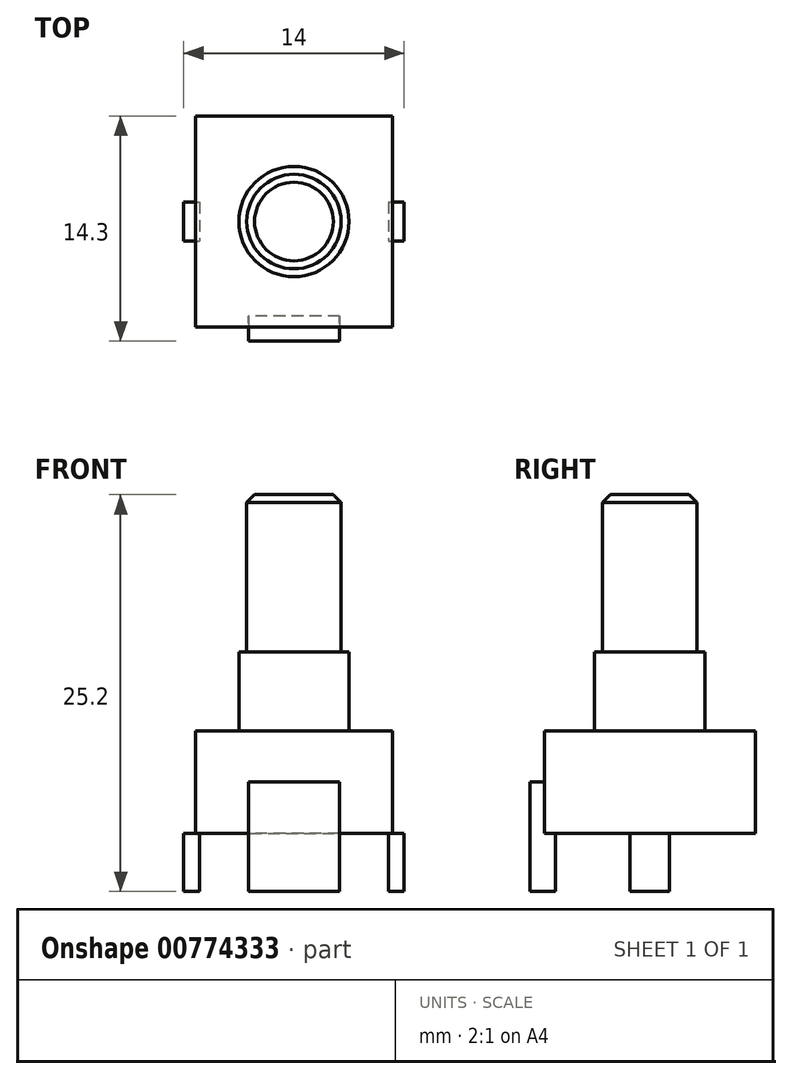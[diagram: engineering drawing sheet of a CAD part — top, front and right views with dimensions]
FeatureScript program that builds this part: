
annotation { "Feature Type Name" : "Feature", "Feature Type Description" : "" }
export const myFeature = defineFeature(function(context is Context, id is Id, definition is map)
    precondition{}
    {
        {
            var Q0;
            Q0=qCreatedBy(makeId("Top.planeOp"),FACE);
            var sketch = newSketch(context, id + "F0", { "sketchPlane" : qUnion([Q0])});
            skLineSegment(sketch, "E0", {"start": v(-6.25, 11.7) * mm, "end": v(0, 11.7) * mm});
            skLineSegment(sketch, "E1", {"start": v(0, 11.7) * mm, "end": v(6.25, 11.7) * mm});
            skLineSegment(sketch, "E2", {"start": v(6.25, 11.7) * mm, "end": v(6.25, 5) * mm});
            skLineSegment(sketch, "E3", {"start": v(6.25, 5) * mm, "end": v(6.25, -1.7) * mm});
            skLineSegment(sketch, "E4", {"start": v(-6.25, 11.7) * mm, "end": v(-6.25, -1.7) * mm});
            skLineSegment(sketch, "E5", {"start": v(-6.25, -1.7) * mm, "end": v(6.25, -1.7) * mm});
            skPoint(sketch, "E6", {"position": v(0, 5) * mm});
            skSolve(sketch);
        }
        {
            var Q0;
            Q0=qCreatedBy(makeId("Top.planeOp"),FACE);
            var sketch = newSketch(context, id + "F1", { "sketchPlane" : qUnion([Q0])});
            skCircle(sketch, "E7", {"center": v(0, 5) * mm, "radius": 3.5 * mm});
            skSolve(sketch);
        }
        {
            var Q0;
            Q0=qCreatedBy(makeId("Top.planeOp"),FACE);
            var sketch = newSketch(context, id + "F2", { "sketchPlane" : qUnion([Q0])});
            skCircle(sketch, "E8", {"center": v(0, 5) * mm, "radius": 3 * mm});
            skSolve(sketch);
        }
        {
            var Q0;
            Q0 = qSketchRegion(id + "F0", true);
            extrude(context, id + "F3", {"entities" : qUnion([Q0]), "depth" : 6.5 * mm, "offsetDistance" : 25 * mm});
        }
        {
            var Q0;
            Q0 = qSketchRegion(id + "F1", true);
            extrude(context, id + "F4", {"entities" : qUnion([Q0]), "operationType" : NewBodyOperationType.ADD, "depth" : (6.5 + 5) * mm, "offsetDistance" : 25 * mm});
        }
        {
            var Q0;
            Q0 = qSketchRegion(id + "F2", true);
            extrude(context, id + "F5", {"entities" : qUnion([Q0]), "operationType" : NewBodyOperationType.ADD, "depth" : (6.5 + 15) * mm, "offsetDistance" : 25 * mm});
        }
        {
            var Q0;
            Q0=makeQuery(id+"F5.opExtrude","CAP_EDGE",EDGE,{"disambiguationData":[OSD([sQuery(id+"F2.wireOp",EDGE,"E8")])],"isStart":false});
            chamfer(context, id + "F6", {"entities" : qUnion([Q0]), "width" : 0.5 * mm, "tangentPropagation" : true});
        }
        {
            var Q0;
            Q0=qCreatedBy(makeId("Top.planeOp"),FACE);
            var sketch = newSketch(context, id + "F7", { "sketchPlane" : qUnion([Q0])});
            skLineSegment(sketch, "E9.bottom", {"start": v(-7, 6.25) * mm, "end": v(-6, 6.25) * mm});
            skLineSegment(sketch, "E9.top", {"start": v(-7, 3.75) * mm, "end": v(-6, 3.75) * mm});
            skLineSegment(sketch, "E9.left", {"start": v(-7, 6.25) * mm, "end": v(-7, 3.75) * mm});
            skLineSegment(sketch, "E9.right", {"start": v(-6, 6.25) * mm, "end": v(-6, 3.75) * mm});
            skLineSegment(sketch, "E10.bottom", {"start": v(6, 6.25) * mm, "end": v(7, 6.25) * mm});
            skLineSegment(sketch, "E10.top", {"start": v(6, 3.75) * mm, "end": v(7, 3.75) * mm});
            skLineSegment(sketch, "E10.left", {"start": v(6, 6.25) * mm, "end": v(6, 3.75) * mm});
            skLineSegment(sketch, "E10.right", {"start": v(7, 6.25) * mm, "end": v(7, 3.75) * mm});
            skSolve(sketch);
        }
        {
            var Q0;
            Q0 = qSketchRegion(id + "F7", true);
            extrude(context, id + "F8", {"entities" : qUnion([Q0]), "operationType" : NewBodyOperationType.ADD, "oppositeDirection" : true, "depth" : 3.7 * mm, "offsetDistance" : 25 * mm});
        }
        {
            var Q0;
            Q0=qCreatedBy(makeId("Top.planeOp"),FACE);
            var sketch = newSketch(context, id + "F9", { "sketchPlane" : qUnion([Q0])});
            skLineSegment(sketch, "E11.bottom", {"start": v(-2.9, -2.6) * mm, "end": v(2.9, -2.6) * mm});
            skLineSegment(sketch, "E11.top", {"start": v(-2.9, -1) * mm, "end": v(2.9, -1) * mm});
            skLineSegment(sketch, "E11.left", {"start": v(-2.9, -2.6) * mm, "end": v(-2.9, -1) * mm});
            skLineSegment(sketch, "E11.right", {"start": v(2.9, -2.6) * mm, "end": v(2.9, -1) * mm});
            skSolve(sketch);
        }
        {
            var Q0;
            Q0 = qSketchRegion(id + "F9", true);
            extrude(context, id + "F10", {"entities" : qUnion([Q0]), "operationType" : NewBodyOperationType.ADD, "depth" : 3.25 * mm, "offsetDistance" : 25 * mm, "hasSecondDirection" : true, "secondDirectionOppositeDirection" : true, "secondDirectionDepth" : 3.7 * mm});
        }
    });
